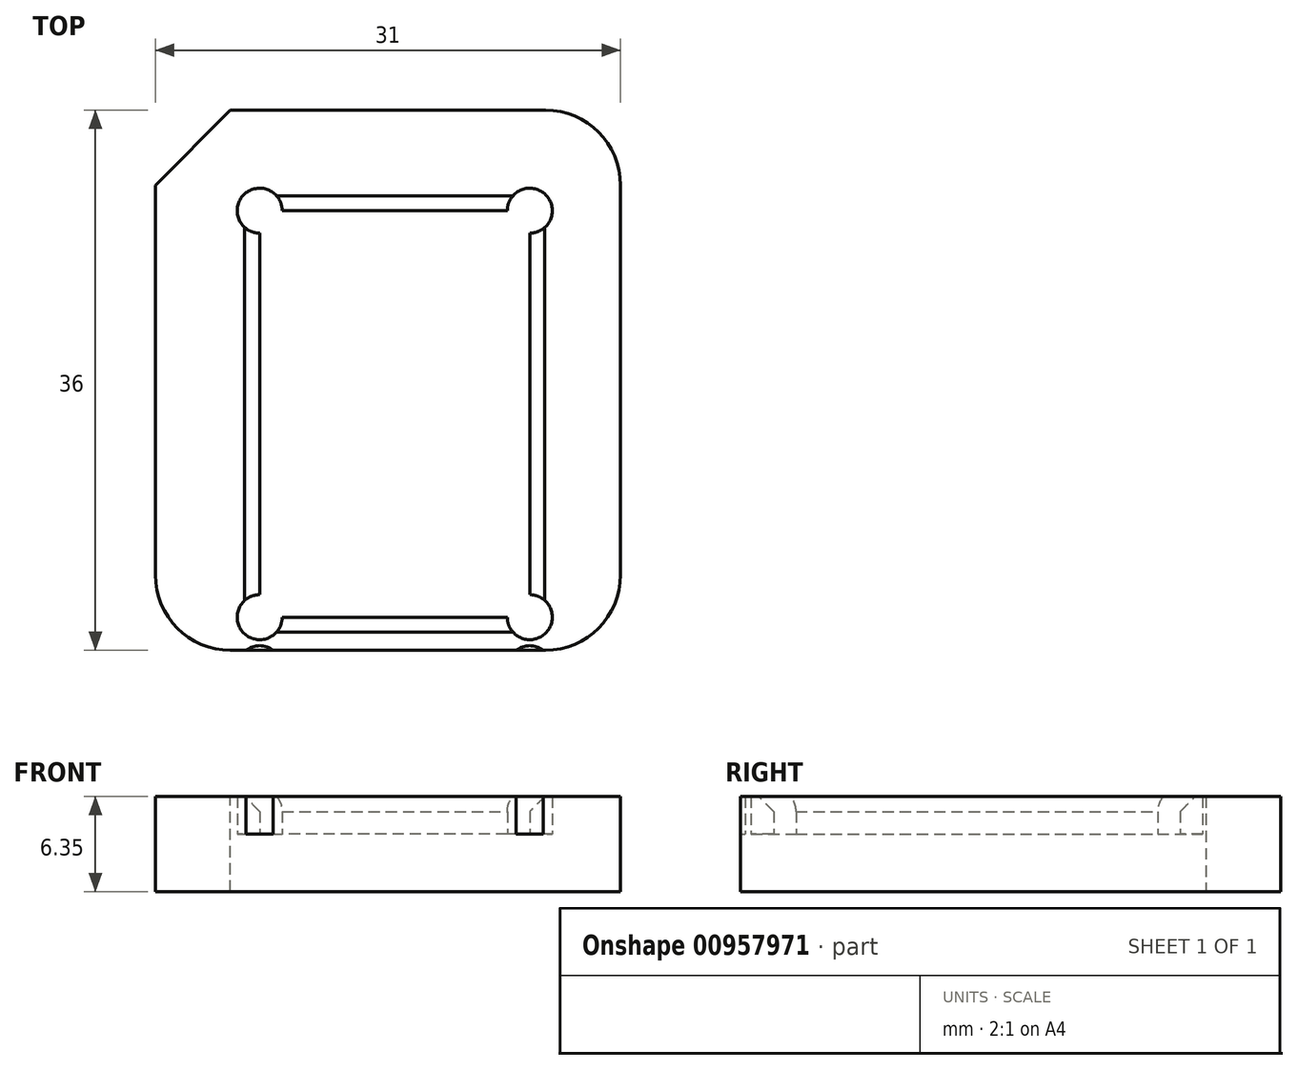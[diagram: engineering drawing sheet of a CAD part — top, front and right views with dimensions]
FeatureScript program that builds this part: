
annotation { "Feature Type Name" : "Feature", "Feature Type Description" : "" }
export const myFeature = defineFeature(function(context is Context, id is Id, definition is map)
    precondition{}
    {
        {
            var Q0;
            Q0=qCreatedBy(makeId("Top.planeOp"),FACE);
            var sketch = newSketch(context, id + "F0", { "sketchPlane" : qUnion([Q0])});
            skLineSegment(sketch, "E0.bottom", {"start": v(0, 0) * mm, "end": v(31, 0) * mm});
            skLineSegment(sketch, "E0.top", {"start": v(0, -36) * mm, "end": v(31, -36) * mm});
            skLineSegment(sketch, "E0.left", {"start": v(0, 0) * mm, "end": v(0, -36) * mm});
            skLineSegment(sketch, "E0.right", {"start": v(31, 0) * mm, "end": v(31, -36) * mm});
            skSolve(sketch);
        }
        {
            var Q0;
            Q0=makeQuery(id+"F0.imprint","IMPRINT",FACE,{"disambiguationData":[TD([[makeQuery(id+"F0.imprint","IMPRINT",EDGE,{"derivedFrom":sQuery(id+"F0.wireOp",EDGE,"E0.bottom")}),-1.0]])]});
            extrude(context, id + "F1", {"entities" : qUnion([Q0]), "depth" : 3.85 * mm, "offsetDistance" : 25 * mm});
        }
        {
            var Q0;
            Q0=makeQuery(id+"F1.opExtrude","SWEPT_EDGE",EDGE,{"disambiguationData":[OSD([sQuery(id+"F0.wireOp",EDGE,"E0.bottom"),sQuery(id+"F0.wireOp",EDGE,"E0.left")])]});
            chamfer(context, id + "F2", {"entities" : qUnion([Q0]), "chamferType" : ChamferType.OFFSET_ANGLE, "width" : 5 * mm, "oppositeDirection" : false, "angle" : 45 * degree, "tangentPropagation" : true});
        }
        {
            var Q0;
            {var subQ0=sQuery(id+"F0.wireOp",EDGE,"E0.right");var subQ1=sQuery(id+"F0.wireOp",EDGE,"E0.bottom");Q0=makeQuery(id+"F5.boolean.opBoolean","MERGE",EDGE,{"derivedFrom":[makeQuery(id+"F1.opExtrude","SWEPT_EDGE",EDGE,{"disambiguationData":[OSD([subQ1,subQ0])]}),makeQuery(id+"F5.opExtrude","SWEPT_EDGE",EDGE,{"disambiguationData":[OSD([subQ1,subQ0])]})]});}
            var Q1;
            {var subQ0=sQuery(id+"F0.wireOp",EDGE,"E0.right");var subQ1=sQuery(id+"F0.wireOp",EDGE,"E0.top");Q1=makeQuery(id+"F5.boolean.opBoolean","MERGE",EDGE,{"derivedFrom":[makeQuery(id+"F1.opExtrude","SWEPT_EDGE",EDGE,{"disambiguationData":[OSD([subQ1,subQ0])]}),makeQuery(id+"F5.opExtrude","SWEPT_EDGE",EDGE,{"disambiguationData":[OSD([subQ1,subQ0])]})]});}
            var Q2;
            {var subQ0=sQuery(id+"F0.wireOp",EDGE,"E0.left");var subQ1=sQuery(id+"F0.wireOp",EDGE,"E0.top");Q2=makeQuery(id+"F5.boolean.opBoolean","MERGE",EDGE,{"derivedFrom":[makeQuery(id+"F1.opExtrude","SWEPT_EDGE",EDGE,{"disambiguationData":[OSD([subQ1,subQ0])]}),makeQuery(id+"F5.opExtrude","SWEPT_EDGE",EDGE,{"disambiguationData":[OSD([subQ1,subQ0])]})]});}
            fillet(context, id + "F3", {"entities" : qUnion([Q0, Q1, Q2]), "radius" : 5 * mm, "tangentPropagation" : true, "allowEdgeOverflow" : false});
        }
        {
            var Q0;
            Q0=makeQuery(id+"F1.opExtrude","CAP_FACE",FACE,{"disambiguationData":[OSD([sQuery(id+"F0.wireOp",EDGE,"E0.bottom"),sQuery(id+"F0.wireOp",EDGE,"E0.top"),sQuery(id+"F0.wireOp",EDGE,"E0.left"),sQuery(id+"F0.wireOp",EDGE,"E0.right")])],"isStart":false});
            var sketch = newSketch(context, id + "F4", { "sketchPlane" : qUnion([Q0])});
            skLineSegment(sketch, "E1.bottom", {"start": v(24.95, -33.8) * mm, "end": v(6.95, -33.8) * mm});
            skLineSegment(sketch, "E1.top", {"start": v(24.95, -6.7) * mm, "end": v(6.95, -6.7) * mm});
            skLineSegment(sketch, "E1.left", {"start": v(24.95, -33.8) * mm, "end": v(24.95, -6.7) * mm});
            skLineSegment(sketch, "E1.right", {"start": v(6.95, -33.8) * mm, "end": v(6.95, -6.7) * mm});
            skPoint(sketch, "E1.middle", {"position": v(15.95, -20.25) * mm});
            skCircle(sketch, "E2", {"center": v(6.95, -6.7) * mm, "radius": 1.5 * mm});
            skCircle(sketch, "E3", {"center": v(24.95, -6.7) * mm, "radius": 1.5 * mm});
            skCircle(sketch, "E4", {"center": v(24.95, -33.8) * mm, "radius": 1.5 * mm});
            skCircle(sketch, "E5", {"center": v(6.95, -33.8) * mm, "radius": 1.5 * mm});
            skLineSegment(sketch, "E6.0.1.0", {"start": v(24.95, -64.3) * mm, "end": v(6.95, -64.3) * mm});
            skCircle(sketch, "E6.0.1.1", {"center": v(6.95, -64.3) * mm, "radius": 1.5 * mm});
            skLineSegment(sketch, "E6.0.1.2", {"start": v(6.95, -64.3) * mm, "end": v(6.95, -37.2) * mm});
            skCircle(sketch, "E6.0.1.3", {"center": v(6.95, -37.2) * mm, "radius": 1.5 * mm});
            skLineSegment(sketch, "E6.0.1.4", {"start": v(24.95, -37.2) * mm, "end": v(6.95, -37.2) * mm});
            skCircle(sketch, "E6.0.1.5", {"center": v(24.95, -37.2) * mm, "radius": 1.5 * mm});
            skLineSegment(sketch, "E6.0.1.6", {"start": v(24.95, -64.3) * mm, "end": v(24.95, -37.2) * mm});
            skCircle(sketch, "E6.0.1.7", {"center": v(24.95, -64.3) * mm, "radius": 1.5 * mm});
            skLineSegment(sketch, "E6.0.2.0", {"start": v(24.95, -94.8) * mm, "end": v(6.95, -94.8) * mm});
            skCircle(sketch, "E6.0.2.1", {"center": v(6.95, -94.8) * mm, "radius": 1.5 * mm});
            skLineSegment(sketch, "E6.0.2.2", {"start": v(6.95, -94.8) * mm, "end": v(6.95, -67.7) * mm});
            skCircle(sketch, "E6.0.2.3", {"center": v(6.95, -67.7) * mm, "radius": 1.5 * mm});
            skLineSegment(sketch, "E6.0.2.4", {"start": v(24.95, -67.7) * mm, "end": v(6.95, -67.7) * mm});
            skCircle(sketch, "E6.0.2.5", {"center": v(24.95, -67.7) * mm, "radius": 1.5 * mm});
            skLineSegment(sketch, "E6.0.2.6", {"start": v(24.95, -94.8) * mm, "end": v(24.95, -67.7) * mm});
            skCircle(sketch, "E6.0.2.7", {"center": v(24.95, -94.8) * mm, "radius": 1.5 * mm});
            skLineSegment(sketch, "E6.0.3.0", {"start": v(24.95, -125.3) * mm, "end": v(6.95, -125.3) * mm});
            skCircle(sketch, "E6.0.3.1", {"center": v(6.95, -125.3) * mm, "radius": 1.5 * mm});
            skLineSegment(sketch, "E6.0.3.2", {"start": v(6.95, -125.3) * mm, "end": v(6.95, -98.2) * mm});
            skCircle(sketch, "E6.0.3.3", {"center": v(6.95, -98.2) * mm, "radius": 1.5 * mm});
            skLineSegment(sketch, "E6.0.3.4", {"start": v(24.95, -98.2) * mm, "end": v(6.95, -98.2) * mm});
            skCircle(sketch, "E6.0.3.5", {"center": v(24.95, -98.2) * mm, "radius": 1.5 * mm});
            skLineSegment(sketch, "E6.0.3.6", {"start": v(24.95, -125.3) * mm, "end": v(24.95, -98.2) * mm});
            skCircle(sketch, "E6.0.3.7", {"center": v(24.95, -125.3) * mm, "radius": 1.5 * mm});
            skLineSegment(sketch, "E6.0.4.0", {"start": v(24.95, -155.8) * mm, "end": v(6.95, -155.8) * mm});
            skCircle(sketch, "E6.0.4.1", {"center": v(6.95, -155.8) * mm, "radius": 1.5 * mm});
            skLineSegment(sketch, "E6.0.4.2", {"start": v(6.95, -155.8) * mm, "end": v(6.95, -128.7) * mm});
            skCircle(sketch, "E6.0.4.3", {"center": v(6.95, -128.7) * mm, "radius": 1.5 * mm});
            skLineSegment(sketch, "E6.0.4.4", {"start": v(24.95, -128.7) * mm, "end": v(6.95, -128.7) * mm});
            skCircle(sketch, "E6.0.4.5", {"center": v(24.95, -128.7) * mm, "radius": 1.5 * mm});
            skLineSegment(sketch, "E6.0.4.6", {"start": v(24.95, -155.8) * mm, "end": v(24.95, -128.7) * mm});
            skCircle(sketch, "E6.0.4.7", {"center": v(24.95, -155.8) * mm, "radius": 1.5 * mm});
            skLineSegment(sketch, "E6.0.5.0", {"start": v(24.95, -186.3) * mm, "end": v(6.95, -186.3) * mm});
            skCircle(sketch, "E6.0.5.1", {"center": v(6.95, -186.3) * mm, "radius": 1.5 * mm});
            skLineSegment(sketch, "E6.0.5.2", {"start": v(6.95, -186.3) * mm, "end": v(6.95, -159.2) * mm});
            skCircle(sketch, "E6.0.5.3", {"center": v(6.95, -159.2) * mm, "radius": 1.5 * mm});
            skLineSegment(sketch, "E6.0.5.4", {"start": v(24.95, -159.2) * mm, "end": v(6.95, -159.2) * mm});
            skCircle(sketch, "E6.0.5.5", {"center": v(24.95, -159.2) * mm, "radius": 1.5 * mm});
            skLineSegment(sketch, "E6.0.5.6", {"start": v(24.95, -186.3) * mm, "end": v(24.95, -159.2) * mm});
            skCircle(sketch, "E6.0.5.7", {"center": v(24.95, -186.3) * mm, "radius": 1.5 * mm});
            skLineSegment(sketch, "E6.0.6.0", {"start": v(24.95, -216.8) * mm, "end": v(6.95, -216.8) * mm});
            skCircle(sketch, "E6.0.6.1", {"center": v(6.95, -216.8) * mm, "radius": 1.5 * mm});
            skLineSegment(sketch, "E6.0.6.2", {"start": v(6.95, -216.8) * mm, "end": v(6.95, -189.7) * mm});
            skCircle(sketch, "E6.0.6.3", {"center": v(6.95, -189.7) * mm, "radius": 1.5 * mm});
            skLineSegment(sketch, "E6.0.6.4", {"start": v(24.95, -189.7) * mm, "end": v(6.95, -189.7) * mm});
            skCircle(sketch, "E6.0.6.5", {"center": v(24.95, -189.7) * mm, "radius": 1.5 * mm});
            skLineSegment(sketch, "E6.0.6.6", {"start": v(24.95, -216.8) * mm, "end": v(24.95, -189.7) * mm});
            skCircle(sketch, "E6.0.6.7", {"center": v(24.95, -216.8) * mm, "radius": 1.5 * mm});
            skLineSegment(sketch, "E6.0.7.0", {"start": v(24.95, -247.3) * mm, "end": v(6.95, -247.3) * mm});
            skCircle(sketch, "E6.0.7.1", {"center": v(6.95, -247.3) * mm, "radius": 1.5 * mm});
            skLineSegment(sketch, "E6.0.7.2", {"start": v(6.95, -247.3) * mm, "end": v(6.95, -220.2) * mm});
            skCircle(sketch, "E6.0.7.3", {"center": v(6.95, -220.2) * mm, "radius": 1.5 * mm});
            skLineSegment(sketch, "E6.0.7.4", {"start": v(24.95, -220.2) * mm, "end": v(6.95, -220.2) * mm});
            skCircle(sketch, "E6.0.7.5", {"center": v(24.95, -220.2) * mm, "radius": 1.5 * mm});
            skLineSegment(sketch, "E6.0.7.6", {"start": v(24.95, -247.3) * mm, "end": v(24.95, -220.2) * mm});
            skCircle(sketch, "E6.0.7.7", {"center": v(24.95, -247.3) * mm, "radius": 1.5 * mm});
            skLineSegment(sketch, "E6.0.8.0", {"start": v(24.95, -277.8) * mm, "end": v(6.95, -277.8) * mm});
            skCircle(sketch, "E6.0.8.1", {"center": v(6.95, -277.8) * mm, "radius": 1.5 * mm});
            skLineSegment(sketch, "E6.0.8.2", {"start": v(6.95, -277.8) * mm, "end": v(6.95, -250.7) * mm});
            skCircle(sketch, "E6.0.8.3", {"center": v(6.95, -250.7) * mm, "radius": 1.5 * mm});
            skLineSegment(sketch, "E6.0.8.4", {"start": v(24.95, -250.7) * mm, "end": v(6.95, -250.7) * mm});
            skCircle(sketch, "E6.0.8.5", {"center": v(24.95, -250.7) * mm, "radius": 1.5 * mm});
            skLineSegment(sketch, "E6.0.8.6", {"start": v(24.95, -277.8) * mm, "end": v(24.95, -250.7) * mm});
            skCircle(sketch, "E6.0.8.7", {"center": v(24.95, -277.8) * mm, "radius": 1.5 * mm});
            skLineSegment(sketch, "E6.0.9.0", {"start": v(24.95, -308.3) * mm, "end": v(6.95, -308.3) * mm});
            skCircle(sketch, "E6.0.9.1", {"center": v(6.95, -308.3) * mm, "radius": 1.5 * mm});
            skLineSegment(sketch, "E6.0.9.2", {"start": v(6.95, -308.3) * mm, "end": v(6.95, -281.2) * mm});
            skCircle(sketch, "E6.0.9.3", {"center": v(6.95, -281.2) * mm, "radius": 1.5 * mm});
            skLineSegment(sketch, "E6.0.9.4", {"start": v(24.95, -281.2) * mm, "end": v(6.95, -281.2) * mm});
            skCircle(sketch, "E6.0.9.5", {"center": v(24.95, -281.2) * mm, "radius": 1.5 * mm});
            skLineSegment(sketch, "E6.0.9.6", {"start": v(24.95, -308.3) * mm, "end": v(24.95, -281.2) * mm});
            skCircle(sketch, "E6.0.9.7", {"center": v(24.95, -308.3) * mm, "radius": 1.5 * mm});
            skLineSegment(sketch, "E6.1.0.0", {"start": v(50.95, -33.8) * mm, "end": v(32.95, -33.8) * mm});
            skCircle(sketch, "E6.1.0.1", {"center": v(32.95, -33.8) * mm, "radius": 1.5 * mm});
            skLineSegment(sketch, "E6.1.0.2", {"start": v(32.95, -33.8) * mm, "end": v(32.95, -6.7) * mm});
            skCircle(sketch, "E6.1.0.3", {"center": v(32.95, -6.7) * mm, "radius": 1.5 * mm});
            skLineSegment(sketch, "E6.1.0.4", {"start": v(50.95, -6.7) * mm, "end": v(32.95, -6.7) * mm});
            skCircle(sketch, "E6.1.0.5", {"center": v(50.95, -6.7) * mm, "radius": 1.5 * mm});
            skLineSegment(sketch, "E6.1.0.6", {"start": v(50.95, -33.8) * mm, "end": v(50.95, -6.7) * mm});
            skCircle(sketch, "E6.1.0.7", {"center": v(50.95, -33.8) * mm, "radius": 1.5 * mm});
            skLineSegment(sketch, "E6.1.1.0", {"start": v(50.95, -64.3) * mm, "end": v(32.95, -64.3) * mm});
            skCircle(sketch, "E6.1.1.1", {"center": v(32.95, -64.3) * mm, "radius": 1.5 * mm});
            skLineSegment(sketch, "E6.1.1.2", {"start": v(32.95, -64.3) * mm, "end": v(32.95, -37.2) * mm});
            skCircle(sketch, "E6.1.1.3", {"center": v(32.95, -37.2) * mm, "radius": 1.5 * mm});
            skLineSegment(sketch, "E6.1.1.4", {"start": v(50.95, -37.2) * mm, "end": v(32.95, -37.2) * mm});
            skCircle(sketch, "E6.1.1.5", {"center": v(50.95, -37.2) * mm, "radius": 1.5 * mm});
            skLineSegment(sketch, "E6.1.1.6", {"start": v(50.95, -64.3) * mm, "end": v(50.95, -37.2) * mm});
            skCircle(sketch, "E6.1.1.7", {"center": v(50.95, -64.3) * mm, "radius": 1.5 * mm});
            skLineSegment(sketch, "E6.1.2.0", {"start": v(50.95, -94.8) * mm, "end": v(32.95, -94.8) * mm});
            skCircle(sketch, "E6.1.2.1", {"center": v(32.95, -94.8) * mm, "radius": 1.5 * mm});
            skLineSegment(sketch, "E6.1.2.2", {"start": v(32.95, -94.8) * mm, "end": v(32.95, -67.7) * mm});
            skCircle(sketch, "E6.1.2.3", {"center": v(32.95, -67.7) * mm, "radius": 1.5 * mm});
            skLineSegment(sketch, "E6.1.2.4", {"start": v(50.95, -67.7) * mm, "end": v(32.95, -67.7) * mm});
            skCircle(sketch, "E6.1.2.5", {"center": v(50.95, -67.7) * mm, "radius": 1.5 * mm});
            skLineSegment(sketch, "E6.1.2.6", {"start": v(50.95, -94.8) * mm, "end": v(50.95, -67.7) * mm});
            skCircle(sketch, "E6.1.2.7", {"center": v(50.95, -94.8) * mm, "radius": 1.5 * mm});
            skLineSegment(sketch, "E6.1.3.0", {"start": v(50.95, -125.3) * mm, "end": v(32.95, -125.3) * mm});
            skCircle(sketch, "E6.1.3.1", {"center": v(32.95, -125.3) * mm, "radius": 1.5 * mm});
            skLineSegment(sketch, "E6.1.3.2", {"start": v(32.95, -125.3) * mm, "end": v(32.95, -98.2) * mm});
            skCircle(sketch, "E6.1.3.3", {"center": v(32.95, -98.2) * mm, "radius": 1.5 * mm});
            skLineSegment(sketch, "E6.1.3.4", {"start": v(50.95, -98.2) * mm, "end": v(32.95, -98.2) * mm});
            skCircle(sketch, "E6.1.3.5", {"center": v(50.95, -98.2) * mm, "radius": 1.5 * mm});
            skLineSegment(sketch, "E6.1.3.6", {"start": v(50.95, -125.3) * mm, "end": v(50.95, -98.2) * mm});
            skCircle(sketch, "E6.1.3.7", {"center": v(50.95, -125.3) * mm, "radius": 1.5 * mm});
            skLineSegment(sketch, "E6.1.4.0", {"start": v(50.95, -155.8) * mm, "end": v(32.95, -155.8) * mm});
            skCircle(sketch, "E6.1.4.1", {"center": v(32.95, -155.8) * mm, "radius": 1.5 * mm});
            skLineSegment(sketch, "E6.1.4.2", {"start": v(32.95, -155.8) * mm, "end": v(32.95, -128.7) * mm});
            skCircle(sketch, "E6.1.4.3", {"center": v(32.95, -128.7) * mm, "radius": 1.5 * mm});
            skLineSegment(sketch, "E6.1.4.4", {"start": v(50.95, -128.7) * mm, "end": v(32.95, -128.7) * mm});
            skCircle(sketch, "E6.1.4.5", {"center": v(50.95, -128.7) * mm, "radius": 1.5 * mm});
            skLineSegment(sketch, "E6.1.4.6", {"start": v(50.95, -155.8) * mm, "end": v(50.95, -128.7) * mm});
            skCircle(sketch, "E6.1.4.7", {"center": v(50.95, -155.8) * mm, "radius": 1.5 * mm});
            skLineSegment(sketch, "E6.1.5.0", {"start": v(50.95, -186.3) * mm, "end": v(32.95, -186.3) * mm});
            skCircle(sketch, "E6.1.5.1", {"center": v(32.95, -186.3) * mm, "radius": 1.5 * mm});
            skLineSegment(sketch, "E6.1.5.2", {"start": v(32.95, -186.3) * mm, "end": v(32.95, -159.2) * mm});
            skCircle(sketch, "E6.1.5.3", {"center": v(32.95, -159.2) * mm, "radius": 1.5 * mm});
            skLineSegment(sketch, "E6.1.5.4", {"start": v(50.95, -159.2) * mm, "end": v(32.95, -159.2) * mm});
            skCircle(sketch, "E6.1.5.5", {"center": v(50.95, -159.2) * mm, "radius": 1.5 * mm});
            skLineSegment(sketch, "E6.1.5.6", {"start": v(50.95, -186.3) * mm, "end": v(50.95, -159.2) * mm});
            skCircle(sketch, "E6.1.5.7", {"center": v(50.95, -186.3) * mm, "radius": 1.5 * mm});
            skLineSegment(sketch, "E6.1.6.0", {"start": v(50.95, -216.8) * mm, "end": v(32.95, -216.8) * mm});
            skCircle(sketch, "E6.1.6.1", {"center": v(32.95, -216.8) * mm, "radius": 1.5 * mm});
            skLineSegment(sketch, "E6.1.6.2", {"start": v(32.95, -216.8) * mm, "end": v(32.95, -189.7) * mm});
            skCircle(sketch, "E6.1.6.3", {"center": v(32.95, -189.7) * mm, "radius": 1.5 * mm});
            skLineSegment(sketch, "E6.1.6.4", {"start": v(50.95, -189.7) * mm, "end": v(32.95, -189.7) * mm});
            skCircle(sketch, "E6.1.6.5", {"center": v(50.95, -189.7) * mm, "radius": 1.5 * mm});
            skLineSegment(sketch, "E6.1.6.6", {"start": v(50.95, -216.8) * mm, "end": v(50.95, -189.7) * mm});
            skCircle(sketch, "E6.1.6.7", {"center": v(50.95, -216.8) * mm, "radius": 1.5 * mm});
            skLineSegment(sketch, "E6.1.7.0", {"start": v(50.95, -247.3) * mm, "end": v(32.95, -247.3) * mm});
            skCircle(sketch, "E6.1.7.1", {"center": v(32.95, -247.3) * mm, "radius": 1.5 * mm});
            skLineSegment(sketch, "E6.1.7.2", {"start": v(32.95, -247.3) * mm, "end": v(32.95, -220.2) * mm});
            skCircle(sketch, "E6.1.7.3", {"center": v(32.95, -220.2) * mm, "radius": 1.5 * mm});
            skLineSegment(sketch, "E6.1.7.4", {"start": v(50.95, -220.2) * mm, "end": v(32.95, -220.2) * mm});
            skCircle(sketch, "E6.1.7.5", {"center": v(50.95, -220.2) * mm, "radius": 1.5 * mm});
            skLineSegment(sketch, "E6.1.7.6", {"start": v(50.95, -247.3) * mm, "end": v(50.95, -220.2) * mm});
            skCircle(sketch, "E6.1.7.7", {"center": v(50.95, -247.3) * mm, "radius": 1.5 * mm});
            skLineSegment(sketch, "E6.1.8.0", {"start": v(50.95, -277.8) * mm, "end": v(32.95, -277.8) * mm});
            skCircle(sketch, "E6.1.8.1", {"center": v(32.95, -277.8) * mm, "radius": 1.5 * mm});
            skLineSegment(sketch, "E6.1.8.2", {"start": v(32.95, -277.8) * mm, "end": v(32.95, -250.7) * mm});
            skCircle(sketch, "E6.1.8.3", {"center": v(32.95, -250.7) * mm, "radius": 1.5 * mm});
            skLineSegment(sketch, "E6.1.8.4", {"start": v(50.95, -250.7) * mm, "end": v(32.95, -250.7) * mm});
            skCircle(sketch, "E6.1.8.5", {"center": v(50.95, -250.7) * mm, "radius": 1.5 * mm});
            skLineSegment(sketch, "E6.1.8.6", {"start": v(50.95, -277.8) * mm, "end": v(50.95, -250.7) * mm});
            skCircle(sketch, "E6.1.8.7", {"center": v(50.95, -277.8) * mm, "radius": 1.5 * mm});
            skLineSegment(sketch, "E6.1.9.0", {"start": v(50.95, -308.3) * mm, "end": v(32.95, -308.3) * mm});
            skCircle(sketch, "E6.1.9.1", {"center": v(32.95, -308.3) * mm, "radius": 1.5 * mm});
            skLineSegment(sketch, "E6.1.9.2", {"start": v(32.95, -308.3) * mm, "end": v(32.95, -281.2) * mm});
            skCircle(sketch, "E6.1.9.3", {"center": v(32.95, -281.2) * mm, "radius": 1.5 * mm});
            skLineSegment(sketch, "E6.1.9.4", {"start": v(50.95, -281.2) * mm, "end": v(32.95, -281.2) * mm});
            skCircle(sketch, "E6.1.9.5", {"center": v(50.95, -281.2) * mm, "radius": 1.5 * mm});
            skLineSegment(sketch, "E6.1.9.6", {"start": v(50.95, -308.3) * mm, "end": v(50.95, -281.2) * mm});
            skCircle(sketch, "E6.1.9.7", {"center": v(50.95, -308.3) * mm, "radius": 1.5 * mm});
            skLineSegment(sketch, "E6.2.0.0", {"start": v(76.95, -33.8) * mm, "end": v(58.95, -33.8) * mm});
            skCircle(sketch, "E6.2.0.1", {"center": v(58.95, -33.8) * mm, "radius": 1.5 * mm});
            skLineSegment(sketch, "E6.2.0.2", {"start": v(58.95, -33.8) * mm, "end": v(58.95, -6.7) * mm});
            skCircle(sketch, "E6.2.0.3", {"center": v(58.95, -6.7) * mm, "radius": 1.5 * mm});
            skLineSegment(sketch, "E6.2.0.4", {"start": v(76.95, -6.7) * mm, "end": v(58.95, -6.7) * mm});
            skCircle(sketch, "E6.2.0.5", {"center": v(76.95, -6.7) * mm, "radius": 1.5 * mm});
            skLineSegment(sketch, "E6.2.0.6", {"start": v(76.95, -33.8) * mm, "end": v(76.95, -6.7) * mm});
            skCircle(sketch, "E6.2.0.7", {"center": v(76.95, -33.8) * mm, "radius": 1.5 * mm});
            skLineSegment(sketch, "E6.2.1.0", {"start": v(76.95, -64.3) * mm, "end": v(58.95, -64.3) * mm});
            skCircle(sketch, "E6.2.1.1", {"center": v(58.95, -64.3) * mm, "radius": 1.5 * mm});
            skLineSegment(sketch, "E6.2.1.2", {"start": v(58.95, -64.3) * mm, "end": v(58.95, -37.2) * mm});
            skCircle(sketch, "E6.2.1.3", {"center": v(58.95, -37.2) * mm, "radius": 1.5 * mm});
            skLineSegment(sketch, "E6.2.1.4", {"start": v(76.95, -37.2) * mm, "end": v(58.95, -37.2) * mm});
            skCircle(sketch, "E6.2.1.5", {"center": v(76.95, -37.2) * mm, "radius": 1.5 * mm});
            skLineSegment(sketch, "E6.2.1.6", {"start": v(76.95, -64.3) * mm, "end": v(76.95, -37.2) * mm});
            skCircle(sketch, "E6.2.1.7", {"center": v(76.95, -64.3) * mm, "radius": 1.5 * mm});
            skLineSegment(sketch, "E6.2.2.0", {"start": v(76.95, -94.8) * mm, "end": v(58.95, -94.8) * mm});
            skCircle(sketch, "E6.2.2.1", {"center": v(58.95, -94.8) * mm, "radius": 1.5 * mm});
            skLineSegment(sketch, "E6.2.2.2", {"start": v(58.95, -94.8) * mm, "end": v(58.95, -67.7) * mm});
            skCircle(sketch, "E6.2.2.3", {"center": v(58.95, -67.7) * mm, "radius": 1.5 * mm});
            skLineSegment(sketch, "E6.2.2.4", {"start": v(76.95, -67.7) * mm, "end": v(58.95, -67.7) * mm});
            skCircle(sketch, "E6.2.2.5", {"center": v(76.95, -67.7) * mm, "radius": 1.5 * mm});
            skLineSegment(sketch, "E6.2.2.6", {"start": v(76.95, -94.8) * mm, "end": v(76.95, -67.7) * mm});
            skCircle(sketch, "E6.2.2.7", {"center": v(76.95, -94.8) * mm, "radius": 1.5 * mm});
            skLineSegment(sketch, "E6.2.3.0", {"start": v(76.95, -125.3) * mm, "end": v(58.95, -125.3) * mm});
            skCircle(sketch, "E6.2.3.1", {"center": v(58.95, -125.3) * mm, "radius": 1.5 * mm});
            skLineSegment(sketch, "E6.2.3.2", {"start": v(58.95, -125.3) * mm, "end": v(58.95, -98.2) * mm});
            skCircle(sketch, "E6.2.3.3", {"center": v(58.95, -98.2) * mm, "radius": 1.5 * mm});
            skLineSegment(sketch, "E6.2.3.4", {"start": v(76.95, -98.2) * mm, "end": v(58.95, -98.2) * mm});
            skCircle(sketch, "E6.2.3.5", {"center": v(76.95, -98.2) * mm, "radius": 1.5 * mm});
            skLineSegment(sketch, "E6.2.3.6", {"start": v(76.95, -125.3) * mm, "end": v(76.95, -98.2) * mm});
            skCircle(sketch, "E6.2.3.7", {"center": v(76.95, -125.3) * mm, "radius": 1.5 * mm});
            skLineSegment(sketch, "E6.2.4.0", {"start": v(76.95, -155.8) * mm, "end": v(58.95, -155.8) * mm});
            skCircle(sketch, "E6.2.4.1", {"center": v(58.95, -155.8) * mm, "radius": 1.5 * mm});
            skLineSegment(sketch, "E6.2.4.2", {"start": v(58.95, -155.8) * mm, "end": v(58.95, -128.7) * mm});
            skCircle(sketch, "E6.2.4.3", {"center": v(58.95, -128.7) * mm, "radius": 1.5 * mm});
            skLineSegment(sketch, "E6.2.4.4", {"start": v(76.95, -128.7) * mm, "end": v(58.95, -128.7) * mm});
            skCircle(sketch, "E6.2.4.5", {"center": v(76.95, -128.7) * mm, "radius": 1.5 * mm});
            skLineSegment(sketch, "E6.2.4.6", {"start": v(76.95, -155.8) * mm, "end": v(76.95, -128.7) * mm});
            skCircle(sketch, "E6.2.4.7", {"center": v(76.95, -155.8) * mm, "radius": 1.5 * mm});
            skLineSegment(sketch, "E6.2.5.0", {"start": v(76.95, -186.3) * mm, "end": v(58.95, -186.3) * mm});
            skCircle(sketch, "E6.2.5.1", {"center": v(58.95, -186.3) * mm, "radius": 1.5 * mm});
            skLineSegment(sketch, "E6.2.5.2", {"start": v(58.95, -186.3) * mm, "end": v(58.95, -159.2) * mm});
            skCircle(sketch, "E6.2.5.3", {"center": v(58.95, -159.2) * mm, "radius": 1.5 * mm});
            skLineSegment(sketch, "E6.2.5.4", {"start": v(76.95, -159.2) * mm, "end": v(58.95, -159.2) * mm});
            skCircle(sketch, "E6.2.5.5", {"center": v(76.95, -159.2) * mm, "radius": 1.5 * mm});
            skLineSegment(sketch, "E6.2.5.6", {"start": v(76.95, -186.3) * mm, "end": v(76.95, -159.2) * mm});
            skCircle(sketch, "E6.2.5.7", {"center": v(76.95, -186.3) * mm, "radius": 1.5 * mm});
            skLineSegment(sketch, "E6.2.6.0", {"start": v(76.95, -216.8) * mm, "end": v(58.95, -216.8) * mm});
            skCircle(sketch, "E6.2.6.1", {"center": v(58.95, -216.8) * mm, "radius": 1.5 * mm});
            skLineSegment(sketch, "E6.2.6.2", {"start": v(58.95, -216.8) * mm, "end": v(58.95, -189.7) * mm});
            skCircle(sketch, "E6.2.6.3", {"center": v(58.95, -189.7) * mm, "radius": 1.5 * mm});
            skLineSegment(sketch, "E6.2.6.4", {"start": v(76.95, -189.7) * mm, "end": v(58.95, -189.7) * mm});
            skCircle(sketch, "E6.2.6.5", {"center": v(76.95, -189.7) * mm, "radius": 1.5 * mm});
            skLineSegment(sketch, "E6.2.6.6", {"start": v(76.95, -216.8) * mm, "end": v(76.95, -189.7) * mm});
            skCircle(sketch, "E6.2.6.7", {"center": v(76.95, -216.8) * mm, "radius": 1.5 * mm});
            skLineSegment(sketch, "E6.2.7.0", {"start": v(76.95, -247.3) * mm, "end": v(58.95, -247.3) * mm});
            skCircle(sketch, "E6.2.7.1", {"center": v(58.95, -247.3) * mm, "radius": 1.5 * mm});
            skLineSegment(sketch, "E6.2.7.2", {"start": v(58.95, -247.3) * mm, "end": v(58.95, -220.2) * mm});
            skCircle(sketch, "E6.2.7.3", {"center": v(58.95, -220.2) * mm, "radius": 1.5 * mm});
            skLineSegment(sketch, "E6.2.7.4", {"start": v(76.95, -220.2) * mm, "end": v(58.95, -220.2) * mm});
            skCircle(sketch, "E6.2.7.5", {"center": v(76.95, -220.2) * mm, "radius": 1.5 * mm});
            skLineSegment(sketch, "E6.2.7.6", {"start": v(76.95, -247.3) * mm, "end": v(76.95, -220.2) * mm});
            skCircle(sketch, "E6.2.7.7", {"center": v(76.95, -247.3) * mm, "radius": 1.5 * mm});
            skLineSegment(sketch, "E6.2.8.0", {"start": v(76.95, -277.8) * mm, "end": v(58.95, -277.8) * mm});
            skCircle(sketch, "E6.2.8.1", {"center": v(58.95, -277.8) * mm, "radius": 1.5 * mm});
            skLineSegment(sketch, "E6.2.8.2", {"start": v(58.95, -277.8) * mm, "end": v(58.95, -250.7) * mm});
            skCircle(sketch, "E6.2.8.3", {"center": v(58.95, -250.7) * mm, "radius": 1.5 * mm});
            skLineSegment(sketch, "E6.2.8.4", {"start": v(76.95, -250.7) * mm, "end": v(58.95, -250.7) * mm});
            skCircle(sketch, "E6.2.8.5", {"center": v(76.95, -250.7) * mm, "radius": 1.5 * mm});
            skLineSegment(sketch, "E6.2.8.6", {"start": v(76.95, -277.8) * mm, "end": v(76.95, -250.7) * mm});
            skCircle(sketch, "E6.2.8.7", {"center": v(76.95, -277.8) * mm, "radius": 1.5 * mm});
            skLineSegment(sketch, "E6.2.9.0", {"start": v(76.95, -308.3) * mm, "end": v(58.95, -308.3) * mm});
            skCircle(sketch, "E6.2.9.1", {"center": v(58.95, -308.3) * mm, "radius": 1.5 * mm});
            skLineSegment(sketch, "E6.2.9.2", {"start": v(58.95, -308.3) * mm, "end": v(58.95, -281.2) * mm});
            skCircle(sketch, "E6.2.9.3", {"center": v(58.95, -281.2) * mm, "radius": 1.5 * mm});
            skLineSegment(sketch, "E6.2.9.4", {"start": v(76.95, -281.2) * mm, "end": v(58.95, -281.2) * mm});
            skCircle(sketch, "E6.2.9.5", {"center": v(76.95, -281.2) * mm, "radius": 1.5 * mm});
            skLineSegment(sketch, "E6.2.9.6", {"start": v(76.95, -308.3) * mm, "end": v(76.95, -281.2) * mm});
            skCircle(sketch, "E6.2.9.7", {"center": v(76.95, -308.3) * mm, "radius": 1.5 * mm});
            skLineSegment(sketch, "E6.3.0.0", {"start": v(102.95, -33.8) * mm, "end": v(84.95, -33.8) * mm});
            skCircle(sketch, "E6.3.0.1", {"center": v(84.95, -33.8) * mm, "radius": 1.5 * mm});
            skLineSegment(sketch, "E6.3.0.2", {"start": v(84.95, -33.8) * mm, "end": v(84.95, -6.7) * mm});
            skCircle(sketch, "E6.3.0.3", {"center": v(84.95, -6.7) * mm, "radius": 1.5 * mm});
            skLineSegment(sketch, "E6.3.0.4", {"start": v(102.95, -6.7) * mm, "end": v(84.95, -6.7) * mm});
            skCircle(sketch, "E6.3.0.5", {"center": v(102.95, -6.7) * mm, "radius": 1.5 * mm});
            skLineSegment(sketch, "E6.3.0.6", {"start": v(102.95, -33.8) * mm, "end": v(102.95, -6.7) * mm});
            skCircle(sketch, "E6.3.0.7", {"center": v(102.95, -33.8) * mm, "radius": 1.5 * mm});
            skLineSegment(sketch, "E6.3.1.0", {"start": v(102.95, -64.3) * mm, "end": v(84.95, -64.3) * mm});
            skCircle(sketch, "E6.3.1.1", {"center": v(84.95, -64.3) * mm, "radius": 1.5 * mm});
            skLineSegment(sketch, "E6.3.1.2", {"start": v(84.95, -64.3) * mm, "end": v(84.95, -37.2) * mm});
            skCircle(sketch, "E6.3.1.3", {"center": v(84.95, -37.2) * mm, "radius": 1.5 * mm});
            skLineSegment(sketch, "E6.3.1.4", {"start": v(102.95, -37.2) * mm, "end": v(84.95, -37.2) * mm});
            skCircle(sketch, "E6.3.1.5", {"center": v(102.95, -37.2) * mm, "radius": 1.5 * mm});
            skLineSegment(sketch, "E6.3.1.6", {"start": v(102.95, -64.3) * mm, "end": v(102.95, -37.2) * mm});
            skCircle(sketch, "E6.3.1.7", {"center": v(102.95, -64.3) * mm, "radius": 1.5 * mm});
            skLineSegment(sketch, "E6.3.2.0", {"start": v(102.95, -94.8) * mm, "end": v(84.95, -94.8) * mm});
            skCircle(sketch, "E6.3.2.1", {"center": v(84.95, -94.8) * mm, "radius": 1.5 * mm});
            skLineSegment(sketch, "E6.3.2.2", {"start": v(84.95, -94.8) * mm, "end": v(84.95, -67.7) * mm});
            skCircle(sketch, "E6.3.2.3", {"center": v(84.95, -67.7) * mm, "radius": 1.5 * mm});
            skLineSegment(sketch, "E6.3.2.4", {"start": v(102.95, -67.7) * mm, "end": v(84.95, -67.7) * mm});
            skCircle(sketch, "E6.3.2.5", {"center": v(102.95, -67.7) * mm, "radius": 1.5 * mm});
            skLineSegment(sketch, "E6.3.2.6", {"start": v(102.95, -94.8) * mm, "end": v(102.95, -67.7) * mm});
            skCircle(sketch, "E6.3.2.7", {"center": v(102.95, -94.8) * mm, "radius": 1.5 * mm});
            skLineSegment(sketch, "E6.3.3.0", {"start": v(102.95, -125.3) * mm, "end": v(84.95, -125.3) * mm});
            skCircle(sketch, "E6.3.3.1", {"center": v(84.95, -125.3) * mm, "radius": 1.5 * mm});
            skLineSegment(sketch, "E6.3.3.2", {"start": v(84.95, -125.3) * mm, "end": v(84.95, -98.2) * mm});
            skCircle(sketch, "E6.3.3.3", {"center": v(84.95, -98.2) * mm, "radius": 1.5 * mm});
            skLineSegment(sketch, "E6.3.3.4", {"start": v(102.95, -98.2) * mm, "end": v(84.95, -98.2) * mm});
            skCircle(sketch, "E6.3.3.5", {"center": v(102.95, -98.2) * mm, "radius": 1.5 * mm});
            skLineSegment(sketch, "E6.3.3.6", {"start": v(102.95, -125.3) * mm, "end": v(102.95, -98.2) * mm});
            skCircle(sketch, "E6.3.3.7", {"center": v(102.95, -125.3) * mm, "radius": 1.5 * mm});
            skLineSegment(sketch, "E6.3.4.0", {"start": v(102.95, -155.8) * mm, "end": v(84.95, -155.8) * mm});
            skCircle(sketch, "E6.3.4.1", {"center": v(84.95, -155.8) * mm, "radius": 1.5 * mm});
            skLineSegment(sketch, "E6.3.4.2", {"start": v(84.95, -155.8) * mm, "end": v(84.95, -128.7) * mm});
            skCircle(sketch, "E6.3.4.3", {"center": v(84.95, -128.7) * mm, "radius": 1.5 * mm});
            skLineSegment(sketch, "E6.3.4.4", {"start": v(102.95, -128.7) * mm, "end": v(84.95, -128.7) * mm});
            skCircle(sketch, "E6.3.4.5", {"center": v(102.95, -128.7) * mm, "radius": 1.5 * mm});
            skLineSegment(sketch, "E6.3.4.6", {"start": v(102.95, -155.8) * mm, "end": v(102.95, -128.7) * mm});
            skCircle(sketch, "E6.3.4.7", {"center": v(102.95, -155.8) * mm, "radius": 1.5 * mm});
            skLineSegment(sketch, "E6.3.5.0", {"start": v(102.95, -186.3) * mm, "end": v(84.95, -186.3) * mm});
            skCircle(sketch, "E6.3.5.1", {"center": v(84.95, -186.3) * mm, "radius": 1.5 * mm});
            skLineSegment(sketch, "E6.3.5.2", {"start": v(84.95, -186.3) * mm, "end": v(84.95, -159.2) * mm});
            skCircle(sketch, "E6.3.5.3", {"center": v(84.95, -159.2) * mm, "radius": 1.5 * mm});
            skLineSegment(sketch, "E6.3.5.4", {"start": v(102.95, -159.2) * mm, "end": v(84.95, -159.2) * mm});
            skCircle(sketch, "E6.3.5.5", {"center": v(102.95, -159.2) * mm, "radius": 1.5 * mm});
            skLineSegment(sketch, "E6.3.5.6", {"start": v(102.95, -186.3) * mm, "end": v(102.95, -159.2) * mm});
            skCircle(sketch, "E6.3.5.7", {"center": v(102.95, -186.3) * mm, "radius": 1.5 * mm});
            skLineSegment(sketch, "E6.3.6.0", {"start": v(102.95, -216.8) * mm, "end": v(84.95, -216.8) * mm});
            skCircle(sketch, "E6.3.6.1", {"center": v(84.95, -216.8) * mm, "radius": 1.5 * mm});
            skLineSegment(sketch, "E6.3.6.2", {"start": v(84.95, -216.8) * mm, "end": v(84.95, -189.7) * mm});
            skCircle(sketch, "E6.3.6.3", {"center": v(84.95, -189.7) * mm, "radius": 1.5 * mm});
            skLineSegment(sketch, "E6.3.6.4", {"start": v(102.95, -189.7) * mm, "end": v(84.95, -189.7) * mm});
            skCircle(sketch, "E6.3.6.5", {"center": v(102.95, -189.7) * mm, "radius": 1.5 * mm});
            skLineSegment(sketch, "E6.3.6.6", {"start": v(102.95, -216.8) * mm, "end": v(102.95, -189.7) * mm});
            skCircle(sketch, "E6.3.6.7", {"center": v(102.95, -216.8) * mm, "radius": 1.5 * mm});
            skLineSegment(sketch, "E6.3.7.0", {"start": v(102.95, -247.3) * mm, "end": v(84.95, -247.3) * mm});
            skCircle(sketch, "E6.3.7.1", {"center": v(84.95, -247.3) * mm, "radius": 1.5 * mm});
            skLineSegment(sketch, "E6.3.7.2", {"start": v(84.95, -247.3) * mm, "end": v(84.95, -220.2) * mm});
            skCircle(sketch, "E6.3.7.3", {"center": v(84.95, -220.2) * mm, "radius": 1.5 * mm});
            skLineSegment(sketch, "E6.3.7.4", {"start": v(102.95, -220.2) * mm, "end": v(84.95, -220.2) * mm});
            skCircle(sketch, "E6.3.7.5", {"center": v(102.95, -220.2) * mm, "radius": 1.5 * mm});
            skLineSegment(sketch, "E6.3.7.6", {"start": v(102.95, -247.3) * mm, "end": v(102.95, -220.2) * mm});
            skCircle(sketch, "E6.3.7.7", {"center": v(102.95, -247.3) * mm, "radius": 1.5 * mm});
            skLineSegment(sketch, "E6.3.8.0", {"start": v(102.95, -277.8) * mm, "end": v(84.95, -277.8) * mm});
            skCircle(sketch, "E6.3.8.1", {"center": v(84.95, -277.8) * mm, "radius": 1.5 * mm});
            skLineSegment(sketch, "E6.3.8.2", {"start": v(84.95, -277.8) * mm, "end": v(84.95, -250.7) * mm});
            skCircle(sketch, "E6.3.8.3", {"center": v(84.95, -250.7) * mm, "radius": 1.5 * mm});
            skLineSegment(sketch, "E6.3.8.4", {"start": v(102.95, -250.7) * mm, "end": v(84.95, -250.7) * mm});
            skCircle(sketch, "E6.3.8.5", {"center": v(102.95, -250.7) * mm, "radius": 1.5 * mm});
            skLineSegment(sketch, "E6.3.8.6", {"start": v(102.95, -277.8) * mm, "end": v(102.95, -250.7) * mm});
            skCircle(sketch, "E6.3.8.7", {"center": v(102.95, -277.8) * mm, "radius": 1.5 * mm});
            skLineSegment(sketch, "E6.3.9.0", {"start": v(102.95, -308.3) * mm, "end": v(84.95, -308.3) * mm});
            skCircle(sketch, "E6.3.9.1", {"center": v(84.95, -308.3) * mm, "radius": 1.5 * mm});
            skLineSegment(sketch, "E6.3.9.2", {"start": v(84.95, -308.3) * mm, "end": v(84.95, -281.2) * mm});
            skCircle(sketch, "E6.3.9.3", {"center": v(84.95, -281.2) * mm, "radius": 1.5 * mm});
            skLineSegment(sketch, "E6.3.9.4", {"start": v(102.95, -281.2) * mm, "end": v(84.95, -281.2) * mm});
            skCircle(sketch, "E6.3.9.5", {"center": v(102.95, -281.2) * mm, "radius": 1.5 * mm});
            skLineSegment(sketch, "E6.3.9.6", {"start": v(102.95, -308.3) * mm, "end": v(102.95, -281.2) * mm});
            skCircle(sketch, "E6.3.9.7", {"center": v(102.95, -308.3) * mm, "radius": 1.5 * mm});
            skLineSegment(sketch, "E6.4.0.0", {"start": v(128.95, -33.8) * mm, "end": v(110.95, -33.8) * mm});
            skCircle(sketch, "E6.4.0.1", {"center": v(110.95, -33.8) * mm, "radius": 1.5 * mm});
            skLineSegment(sketch, "E6.4.0.2", {"start": v(110.95, -33.8) * mm, "end": v(110.95, -6.7) * mm});
            skCircle(sketch, "E6.4.0.3", {"center": v(110.95, -6.7) * mm, "radius": 1.5 * mm});
            skLineSegment(sketch, "E6.4.0.4", {"start": v(128.95, -6.7) * mm, "end": v(110.95, -6.7) * mm});
            skCircle(sketch, "E6.4.0.5", {"center": v(128.95, -6.7) * mm, "radius": 1.5 * mm});
            skLineSegment(sketch, "E6.4.0.6", {"start": v(128.95, -33.8) * mm, "end": v(128.95, -6.7) * mm});
            skCircle(sketch, "E6.4.0.7", {"center": v(128.95, -33.8) * mm, "radius": 1.5 * mm});
            skLineSegment(sketch, "E6.4.1.0", {"start": v(128.95, -64.3) * mm, "end": v(110.95, -64.3) * mm});
            skCircle(sketch, "E6.4.1.1", {"center": v(110.95, -64.3) * mm, "radius": 1.5 * mm});
            skLineSegment(sketch, "E6.4.1.2", {"start": v(110.95, -64.3) * mm, "end": v(110.95, -37.2) * mm});
            skCircle(sketch, "E6.4.1.3", {"center": v(110.95, -37.2) * mm, "radius": 1.5 * mm});
            skLineSegment(sketch, "E6.4.1.4", {"start": v(128.95, -37.2) * mm, "end": v(110.95, -37.2) * mm});
            skCircle(sketch, "E6.4.1.5", {"center": v(128.95, -37.2) * mm, "radius": 1.5 * mm});
            skLineSegment(sketch, "E6.4.1.6", {"start": v(128.95, -64.3) * mm, "end": v(128.95, -37.2) * mm});
            skCircle(sketch, "E6.4.1.7", {"center": v(128.95, -64.3) * mm, "radius": 1.5 * mm});
            skLineSegment(sketch, "E6.4.2.0", {"start": v(128.95, -94.8) * mm, "end": v(110.95, -94.8) * mm});
            skCircle(sketch, "E6.4.2.1", {"center": v(110.95, -94.8) * mm, "radius": 1.5 * mm});
            skLineSegment(sketch, "E6.4.2.2", {"start": v(110.95, -94.8) * mm, "end": v(110.95, -67.7) * mm});
            skCircle(sketch, "E6.4.2.3", {"center": v(110.95, -67.7) * mm, "radius": 1.5 * mm});
            skLineSegment(sketch, "E6.4.2.4", {"start": v(128.95, -67.7) * mm, "end": v(110.95, -67.7) * mm});
            skCircle(sketch, "E6.4.2.5", {"center": v(128.95, -67.7) * mm, "radius": 1.5 * mm});
            skLineSegment(sketch, "E6.4.2.6", {"start": v(128.95, -94.8) * mm, "end": v(128.95, -67.7) * mm});
            skCircle(sketch, "E6.4.2.7", {"center": v(128.95, -94.8) * mm, "radius": 1.5 * mm});
            skLineSegment(sketch, "E6.4.3.0", {"start": v(128.95, -125.3) * mm, "end": v(110.95, -125.3) * mm});
            skCircle(sketch, "E6.4.3.1", {"center": v(110.95, -125.3) * mm, "radius": 1.5 * mm});
            skLineSegment(sketch, "E6.4.3.2", {"start": v(110.95, -125.3) * mm, "end": v(110.95, -98.2) * mm});
            skCircle(sketch, "E6.4.3.3", {"center": v(110.95, -98.2) * mm, "radius": 1.5 * mm});
            skLineSegment(sketch, "E6.4.3.4", {"start": v(128.95, -98.2) * mm, "end": v(110.95, -98.2) * mm});
            skCircle(sketch, "E6.4.3.5", {"center": v(128.95, -98.2) * mm, "radius": 1.5 * mm});
            skLineSegment(sketch, "E6.4.3.6", {"start": v(128.95, -125.3) * mm, "end": v(128.95, -98.2) * mm});
            skCircle(sketch, "E6.4.3.7", {"center": v(128.95, -125.3) * mm, "radius": 1.5 * mm});
            skLineSegment(sketch, "E6.4.4.0", {"start": v(128.95, -155.8) * mm, "end": v(110.95, -155.8) * mm});
            skCircle(sketch, "E6.4.4.1", {"center": v(110.95, -155.8) * mm, "radius": 1.5 * mm});
            skLineSegment(sketch, "E6.4.4.2", {"start": v(110.95, -155.8) * mm, "end": v(110.95, -128.7) * mm});
            skCircle(sketch, "E6.4.4.3", {"center": v(110.95, -128.7) * mm, "radius": 1.5 * mm});
            skLineSegment(sketch, "E6.4.4.4", {"start": v(128.95, -128.7) * mm, "end": v(110.95, -128.7) * mm});
            skCircle(sketch, "E6.4.4.5", {"center": v(128.95, -128.7) * mm, "radius": 1.5 * mm});
            skLineSegment(sketch, "E6.4.4.6", {"start": v(128.95, -155.8) * mm, "end": v(128.95, -128.7) * mm});
            skCircle(sketch, "E6.4.4.7", {"center": v(128.95, -155.8) * mm, "radius": 1.5 * mm});
            skLineSegment(sketch, "E6.4.5.0", {"start": v(128.95, -186.3) * mm, "end": v(110.95, -186.3) * mm});
            skCircle(sketch, "E6.4.5.1", {"center": v(110.95, -186.3) * mm, "radius": 1.5 * mm});
            skLineSegment(sketch, "E6.4.5.2", {"start": v(110.95, -186.3) * mm, "end": v(110.95, -159.2) * mm});
            skCircle(sketch, "E6.4.5.3", {"center": v(110.95, -159.2) * mm, "radius": 1.5 * mm});
            skLineSegment(sketch, "E6.4.5.4", {"start": v(128.95, -159.2) * mm, "end": v(110.95, -159.2) * mm});
            skCircle(sketch, "E6.4.5.5", {"center": v(128.95, -159.2) * mm, "radius": 1.5 * mm});
            skLineSegment(sketch, "E6.4.5.6", {"start": v(128.95, -186.3) * mm, "end": v(128.95, -159.2) * mm});
            skCircle(sketch, "E6.4.5.7", {"center": v(128.95, -186.3) * mm, "radius": 1.5 * mm});
            skLineSegment(sketch, "E6.4.6.0", {"start": v(128.95, -216.8) * mm, "end": v(110.95, -216.8) * mm});
            skCircle(sketch, "E6.4.6.1", {"center": v(110.95, -216.8) * mm, "radius": 1.5 * mm});
            skLineSegment(sketch, "E6.4.6.2", {"start": v(110.95, -216.8) * mm, "end": v(110.95, -189.7) * mm});
            skCircle(sketch, "E6.4.6.3", {"center": v(110.95, -189.7) * mm, "radius": 1.5 * mm});
            skLineSegment(sketch, "E6.4.6.4", {"start": v(128.95, -189.7) * mm, "end": v(110.95, -189.7) * mm});
            skCircle(sketch, "E6.4.6.5", {"center": v(128.95, -189.7) * mm, "radius": 1.5 * mm});
            skLineSegment(sketch, "E6.4.6.6", {"start": v(128.95, -216.8) * mm, "end": v(128.95, -189.7) * mm});
            skCircle(sketch, "E6.4.6.7", {"center": v(128.95, -216.8) * mm, "radius": 1.5 * mm});
            skLineSegment(sketch, "E6.4.7.0", {"start": v(128.95, -247.3) * mm, "end": v(110.95, -247.3) * mm});
            skCircle(sketch, "E6.4.7.1", {"center": v(110.95, -247.3) * mm, "radius": 1.5 * mm});
            skLineSegment(sketch, "E6.4.7.2", {"start": v(110.95, -247.3) * mm, "end": v(110.95, -220.2) * mm});
            skCircle(sketch, "E6.4.7.3", {"center": v(110.95, -220.2) * mm, "radius": 1.5 * mm});
            skLineSegment(sketch, "E6.4.7.4", {"start": v(128.95, -220.2) * mm, "end": v(110.95, -220.2) * mm});
            skCircle(sketch, "E6.4.7.5", {"center": v(128.95, -220.2) * mm, "radius": 1.5 * mm});
            skLineSegment(sketch, "E6.4.7.6", {"start": v(128.95, -247.3) * mm, "end": v(128.95, -220.2) * mm});
            skCircle(sketch, "E6.4.7.7", {"center": v(128.95, -247.3) * mm, "radius": 1.5 * mm});
            skLineSegment(sketch, "E6.4.8.0", {"start": v(128.95, -277.8) * mm, "end": v(110.95, -277.8) * mm});
            skCircle(sketch, "E6.4.8.1", {"center": v(110.95, -277.8) * mm, "radius": 1.5 * mm});
            skLineSegment(sketch, "E6.4.8.2", {"start": v(110.95, -277.8) * mm, "end": v(110.95, -250.7) * mm});
            skCircle(sketch, "E6.4.8.3", {"center": v(110.95, -250.7) * mm, "radius": 1.5 * mm});
            skLineSegment(sketch, "E6.4.8.4", {"start": v(128.95, -250.7) * mm, "end": v(110.95, -250.7) * mm});
            skCircle(sketch, "E6.4.8.5", {"center": v(128.95, -250.7) * mm, "radius": 1.5 * mm});
            skLineSegment(sketch, "E6.4.8.6", {"start": v(128.95, -277.8) * mm, "end": v(128.95, -250.7) * mm});
            skCircle(sketch, "E6.4.8.7", {"center": v(128.95, -277.8) * mm, "radius": 1.5 * mm});
            skLineSegment(sketch, "E6.4.9.0", {"start": v(128.95, -308.3) * mm, "end": v(110.95, -308.3) * mm});
            skCircle(sketch, "E6.4.9.1", {"center": v(110.95, -308.3) * mm, "radius": 1.5 * mm});
            skLineSegment(sketch, "E6.4.9.2", {"start": v(110.95, -308.3) * mm, "end": v(110.95, -281.2) * mm});
            skCircle(sketch, "E6.4.9.3", {"center": v(110.95, -281.2) * mm, "radius": 1.5 * mm});
            skLineSegment(sketch, "E6.4.9.4", {"start": v(128.95, -281.2) * mm, "end": v(110.95, -281.2) * mm});
            skCircle(sketch, "E6.4.9.5", {"center": v(128.95, -281.2) * mm, "radius": 1.5 * mm});
            skLineSegment(sketch, "E6.4.9.6", {"start": v(128.95, -308.3) * mm, "end": v(128.95, -281.2) * mm});
            skCircle(sketch, "E6.4.9.7", {"center": v(128.95, -308.3) * mm, "radius": 1.5 * mm});
            skLineSegment(sketch, "E6.direction1", {"start": v(6.95, -33.8) * mm, "end": v(32.95, -33.8) * mm, "construction": true});
            skLineSegment(sketch, "E6.direction2", {"start": v(6.95, -33.8) * mm, "end": v(6.95, -64.3) * mm, "construction": true});
            skSolve(sketch);
        }
        {
            var Q0;
            {var subQ603=sQuery(id+"F0.wireOp",EDGE,"E0.top");Q0=makeQuery(id+"F4.imprint","IMPRINT",FACE,{"disambiguationData":[TD([[makeQuery(id+"F4.imprint","IMPRINT",EDGE,{"derivedFrom":makeQuery(id+"F1.opExtrude","CAP_EDGE",EDGE,{"disambiguationData":[OSD([subQ603])],"isStart":false})}),1.0]])]});}
            extrude(context, id + "F5", {"entities" : qUnion([Q0]), "operationType" : NewBodyOperationType.ADD, "depth" : 2.5 * mm, "offsetDistance" : 25 * mm});
        }
        {
            var Q0;
            Q0=makeQuery(id+"F5.opExtrude","CAP_EDGE",EDGE,{"disambiguationData":[OSD([sQuery(id+"F4.wireOp",EDGE,"E1.right")])],"isStart":false});
            var Q1;
            Q1=makeQuery(id+"F5.opExtrude","CAP_EDGE",EDGE,{"disambiguationData":[OSD([sQuery(id+"F4.wireOp",EDGE,"E1.top")])],"isStart":false});
            var Q2;
            Q2=makeQuery(id+"F5.opExtrude","CAP_EDGE",EDGE,{"disambiguationData":[OSD([sQuery(id+"F4.wireOp",EDGE,"E1.left")])],"isStart":false});
            var Q3;
            Q3=makeQuery(id+"F5.opExtrude","CAP_EDGE",EDGE,{"disambiguationData":[OSD([sQuery(id+"F4.wireOp",EDGE,"E1.bottom")])],"isStart":false});
            chamfer(context, id + "F6", {"entities" : qUnion([Q0, Q1, Q2, Q3]), "width" : 1 * mm, "tangentPropagation" : true});
        }
    });
